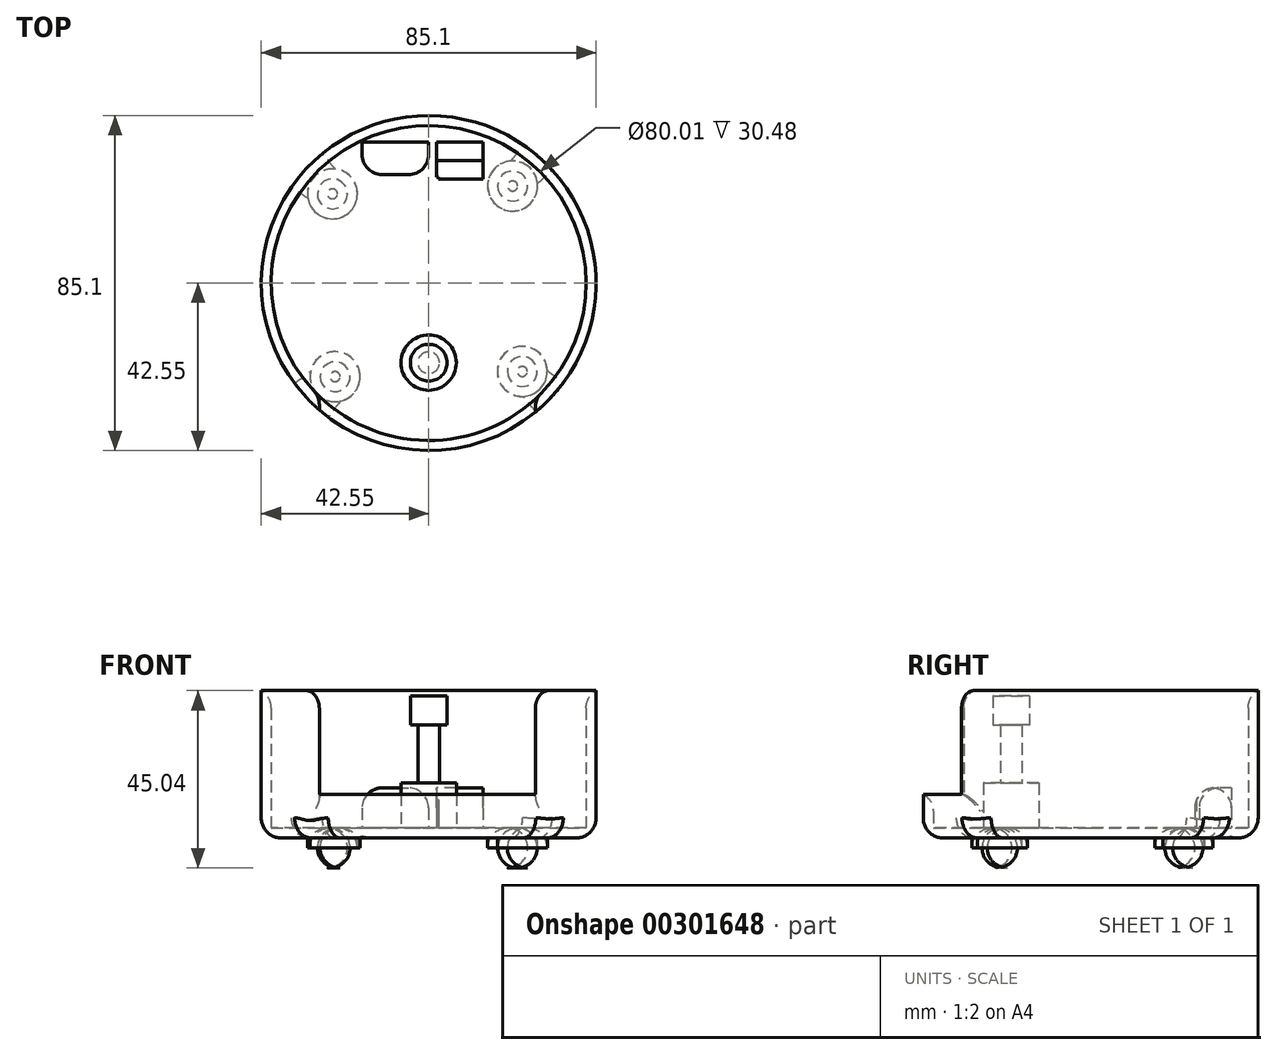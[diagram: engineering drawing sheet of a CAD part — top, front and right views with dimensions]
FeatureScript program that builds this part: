
annotation { "Feature Type Name" : "Feature", "Feature Type Description" : "" }
export const myFeature = defineFeature(function(context is Context, id is Id, definition is map)
    precondition{}
    {
        {
            var Q0;
            Q0=qCreatedBy(makeId("Top.planeOp"),FACE);
            var sketch = newSketch(context, id + "F0", { "sketchPlane" : qUnion([Q0])});
            skCircle(sketch, "E0", {"center": v(0, 0) * mm, "radius": 42.55 * mm});
            skSolve(sketch);
        }
        {
            var Q0;
            Q0 = qSketchRegion(id + "F0", true);
            extrude(context, id + "F1", {"entities" : qUnion([Q0]), "depth" : 38.1 * mm});
        }
        {
            var Q0;
            Q0=makeQuery(id+"F1.opExtrude","CAP_FACE",FACE,{"disambiguationData":[OSD([sQuery(id+"F0.wireOp",EDGE,"E0")])],"isStart":false});
            shell(context, id + "F2", {"entities" : qUnion([Q0]), "thickness" : 2.54 * mm});
        }
        {
            var Q0;
            Q0=qCreatedBy(makeId("Top.planeOp"),FACE);
            var sketch = newSketch(context, id + "F3", { "sketchPlane" : qUnion([Q0])});
            skCircle(sketch, "E1", {"center": v(-23.78, -23.78) * mm, "radius": 6.35 * mm});
            skCircle(sketch, "E2", {"center": v(23.78, -22.45) * mm, "radius": 6.35 * mm});
            skCircle(sketch, "E3", {"center": v(21.34, 24.67) * mm, "radius": 6.35 * mm});
            skCircle(sketch, "E4", {"center": v(-24.45, 22.67) * mm, "radius": 6.35 * mm});
            skSolve(sketch);
        }
        {
            var Q0;
            Q0 = qSketchRegion(id + "F3", true);
            extrude(context, id + "F4", {"entities" : qUnion([Q0]), "operationType" : NewBodyOperationType.ADD, "oppositeDirection" : true, "depth" : 7.62 * mm});
        }
        {
            var Q0;
            Q0=makeQuery(id+"F4.opExtrude","CAP_EDGE",EDGE,{"disambiguationData":[OSD([sQuery(id+"F3.wireOp",EDGE,"E1")])],"isStart":false});
            var Q1;
            Q1=makeQuery(id+"F4.opExtrude","CAP_EDGE",EDGE,{"disambiguationData":[OSD([sQuery(id+"F3.wireOp",EDGE,"E2")])],"isStart":false});
            var Q2;
            Q2=makeQuery(id+"F4.opExtrude","CAP_EDGE",EDGE,{"disambiguationData":[OSD([sQuery(id+"F3.wireOp",EDGE,"E3")])],"isStart":false});
            var Q3;
            Q3=makeQuery(id+"F4.opExtrude","CAP_EDGE",EDGE,{"disambiguationData":[OSD([sQuery(id+"F3.wireOp",EDGE,"E4")])],"isStart":false});
            fillet(context, id + "F5", {"entities" : qUnion([Q0, Q1, Q2, Q3]), "radius" : 5.08 * mm, "tangentPropagation" : true, "allowEdgeOverflow" : false});
        }
        {
            var Q0;
            Q0=qCreatedBy(makeId("Front.planeOp"),FACE);
            cPlane(context, id + "F6", {"entities" : qUnion([Q0]), "cplaneType" : CPlaneType.OFFSET, "offset" : 69.34 * mm, "width" : 152.4 * mm, "height" : 152.4 * mm});
        }
        {
            var Q0;
            Q0=qCreatedBy(id+"F6.planeOp",FACE);
            var sketch = newSketch(context, id + "F7", { "sketchPlane" : qUnion([Q0])});
            skLineSegment(sketch, "E5.bottom", {"start": v(-27.78, 42.9) * mm, "end": v(27.11, 42.9) * mm});
            skLineSegment(sketch, "E5.top", {"start": v(-27.78, 11.11) * mm, "end": v(27.11, 11.11) * mm});
            skLineSegment(sketch, "E5.left", {"start": v(-27.78, 42.9) * mm, "end": v(-27.78, 11.11) * mm});
            skLineSegment(sketch, "E5.right", {"start": v(27.11, 42.9) * mm, "end": v(27.11, 11.11) * mm});
            skSolve(sketch);
        }
        {
            var Q0;
            Q0 = qSketchRegion(id + "F7", true);
            extrude(context, id + "F8", {"entities" : qUnion([Q0]), "operationType" : NewBodyOperationType.REMOVE, "oppositeDirection" : true, "depth" : 55.12 * mm});
        }
        {
            var Q0;
            {var subQ0=sQuery(id+"F0.wireOp",EDGE,"E0");Q0=makeQuery(id+"F8.boolean.opBoolean","INTERSECT",EDGE,{"derivedFrom":[makeQuery(id+"F2.opShell","OFFSET_FACE",FACE,{"disambiguationData":[OSD([subQ0]),TDD([makeQuery(id+"F1.opExtrude","SWEPT_FACE",FACE,{"disambiguationData":[OSD([subQ0])]})])]}),makeQuery(id+"F8.opExtrude","SWEPT_FACE",FACE,{"disambiguationData":[OSD([sQuery(id+"F7.wireOp",EDGE,"E5.top")])]})]});}
            var Q1;
            {var subQ0=sQuery(id+"F0.wireOp",EDGE,"E0");Q1=makeQuery(id+"F8.boolean.opBoolean","INTERSECT",EDGE,{"derivedFrom":[makeQuery(id+"F2.opShell","OFFSET_FACE",FACE,{"disambiguationData":[OSD([subQ0]),TDD([makeQuery(id+"F1.opExtrude","SWEPT_FACE",FACE,{"disambiguationData":[OSD([subQ0])]})])]}),makeQuery(id+"F8.opExtrude","SWEPT_FACE",FACE,{"disambiguationData":[OSD([sQuery(id+"F7.wireOp",EDGE,"E5.left")])]})]});}
            var Q2;
            {var subQ0=sQuery(id+"F0.wireOp",EDGE,"E0");Q2=makeQuery(id+"F8.boolean.opBoolean","INTERSECT",EDGE,{"derivedFrom":[makeQuery(id+"F2.opShell","OFFSET_FACE",FACE,{"disambiguationData":[OSD([subQ0]),TDD([makeQuery(id+"F1.opExtrude","SWEPT_FACE",FACE,{"disambiguationData":[OSD([subQ0])]})])]}),makeQuery(id+"F8.opExtrude","SWEPT_FACE",FACE,{"disambiguationData":[OSD([sQuery(id+"F7.wireOp",EDGE,"E5.right")])]})]});}
            fillet(context, id + "F9", {"entities" : qUnion([Q0, Q1, Q2]), "radius" : 5.08 * mm, "tangentPropagation" : true, "allowEdgeOverflow" : false});
        }
        {
            var Q0;
            {var subQ0=sQuery(id+"F0.wireOp",EDGE,"E0");Q0=makeQuery(id+"F2.opShell","OFFSET_EDGE",EDGE,{"disambiguationData":[OSD([subQ0]),TDD([makeQuery(id+"F1.opExtrude","CAP_EDGE",EDGE,{"disambiguationData":[OSD([subQ0])],"isStart":false})])]});}
            fillet(context, id + "F10", {"entities" : qUnion([Q0]), "radius" : 5.08 * mm, "tangentPropagation" : true, "allowEdgeOverflow" : false});
        }
        {
            var Q0;
            Q0=makeQuery(id+"F1.opExtrude","CAP_EDGE",EDGE,{"disambiguationData":[OSD([sQuery(id+"F0.wireOp",EDGE,"E0")])],"isStart":true});
            fillet(context, id + "F11", {"entities" : qUnion([Q0]), "radius" : 5.08 * mm, "tangentPropagation" : true, "allowEdgeOverflow" : false});
        }
        {
            var Q0;
            Q0=qCreatedBy(makeId("Top.planeOp"),FACE);
            var sketch = newSketch(context, id + "F12", { "sketchPlane" : qUnion([Q0])});
            skLineSegment(sketch, "E6.bottom", {"start": v(-16.9, 35.78) * mm, "end": v(0, 35.78) * mm});
            skLineSegment(sketch, "E6.top", {"start": v(-16.9, 27.56) * mm, "end": v(0, 27.56) * mm});
            skLineSegment(sketch, "E6.left", {"start": v(-16.9, 35.78) * mm, "end": v(-16.9, 27.56) * mm});
            skLineSegment(sketch, "E6.right", {"start": v(0, 35.78) * mm, "end": v(0, 27.56) * mm});
            skLineSegment(sketch, "E7.bottom", {"start": v(2, 35.78) * mm, "end": v(13.78, 35.78) * mm});
            skLineSegment(sketch, "E7.top", {"start": v(2, 35.34) * mm, "end": v(13.78, 35.34) * mm});
            skLineSegment(sketch, "E7.left", {"start": v(2, 35.78) * mm, "end": v(2, 35.34) * mm});
            skLineSegment(sketch, "E7.right", {"start": v(13.78, 35.78) * mm, "end": v(13.78, 35.34) * mm});
            skLineSegment(sketch, "E8.bottom", {"start": v(13.78, 26.45) * mm, "end": v(2.44, 26.45) * mm});
            skLineSegment(sketch, "E8.top", {"start": v(13.78, 26.9) * mm, "end": v(2.44, 26.9) * mm});
            skLineSegment(sketch, "E8.left", {"start": v(13.78, 26.45) * mm, "end": v(13.78, 26.9) * mm});
            skLineSegment(sketch, "E8.right", {"start": v(2.44, 26.45) * mm, "end": v(2.44, 26.9) * mm});
            skLineSegment(sketch, "E9.top", {"start": v(2, 26.9) * mm, "end": v(13.78, 26.9) * mm});
            skLineSegment(sketch, "E9.left", {"start": v(2, 35.34) * mm, "end": v(2, 26.9) * mm});
            skLineSegment(sketch, "E9.right", {"start": v(13.78, 35.34) * mm, "end": v(13.78, 26.9) * mm});
            skSolve(sketch);
        }
        {
            var Q0;
            Q0 = qSketchRegion(id + "F12", true);
            extrude(context, id + "F13", {"entities" : qUnion([Q0]), "operationType" : NewBodyOperationType.ADD, "depth" : 12.7 * mm});
        }
        {
            var Q0;
            Q0=makeQuery(id+"F13.opExtrude","CAP_EDGE",EDGE,{"disambiguationData":[OSD([sQuery(id+"F12.wireOp",EDGE,"E6.top")])],"isStart":false});
            var Q1;
            Q1=makeQuery(id+"F13.opExtrude","SWEPT_EDGE",EDGE,{"disambiguationData":[OSD([sQuery(id+"F12.wireOp",EDGE,"E6.top"),sQuery(id+"F12.wireOp",EDGE,"E6.right")])]});
            var Q2;
            Q2=makeQuery(id+"F13.opExtrude","SWEPT_EDGE",EDGE,{"disambiguationData":[OSD([sQuery(id+"F12.wireOp",EDGE,"E6.top"),sQuery(id+"F12.wireOp",EDGE,"E6.left")])]});
            var Q3;
            Q3=makeQuery(id+"F13.opExtrude","CAP_EDGE",EDGE,{"disambiguationData":[OSD([sQuery(id+"F12.wireOp",EDGE,"E6.left")])],"isStart":false});
            var Q4;
            Q4=makeQuery(id+"F13.opExtrude","CAP_EDGE",EDGE,{"disambiguationData":[OSD([sQuery(id+"F12.wireOp",EDGE,"E6.right")])],"isStart":false});
            fillet(context, id + "F14", {"entities" : qUnion([Q0, Q1, Q2, Q3, Q4]), "radius" : 5.08 * mm, "tangentPropagation" : true, "allowEdgeOverflow" : false});
        }
        {
            var Q0;
            Q0=makeQuery(id+"F13.opExtrude","CAP_EDGE",EDGE,{"disambiguationData":[OSD([sQuery(id+"F12.wireOp",EDGE,"E8.bottom")])],"isStart":false});
            var Q1;
            Q1=makeQuery(id+"F13.opExtrude","CAP_EDGE",EDGE,{"disambiguationData":[OSD([sQuery(id+"F12.wireOp",EDGE,"E7.bottom")])],"isStart":false});
            fillet(context, id + "F15", {"entities" : qUnion([Q0, Q1]), "radius" : 5.08 * mm, "tangentPropagation" : true, "allowEdgeOverflow" : false});
        }
        {
            var Q0;
            {var subQ0=sQuery(id+"F0.wireOp",EDGE,"E0");Q0=makeQuery(id+"F2.opShell","OFFSET_FACE",FACE,{"disambiguationData":[OSD([subQ0]),TDD([makeQuery(id+"F1.opExtrude","CAP_FACE",FACE,{"disambiguationData":[OSD([subQ0])],"isStart":true})])]});}
            var sketch = newSketch(context, id + "F16", { "sketchPlane" : qUnion([Q0])});
            skCircle(sketch, "E10", {"center": v(0, -20.22) * mm, "radius": 7.03 * mm});
            skSolve(sketch);
        }
        {
            var Q0;
            Q0 = qSketchRegion(id + "F16", true);
            extrude(context, id + "F17", {"entities" : qUnion([Q0]), "operationType" : NewBodyOperationType.ADD, "depth" : 11.43 * mm});
        }
        {
            var Q0;
            Q0=makeQuery(id+"F17.opExtrude","CAP_FACE",FACE,{"disambiguationData":[OSD([sQuery(id+"F16.wireOp",EDGE,"E10")])],"isStart":false});
            var sketch = newSketch(context, id + "F18", { "sketchPlane" : qUnion([Q0])});
            skCircle(sketch, "E11", {"center": v(0, -20.22) * mm, "radius": 2.75 * mm});
            skSolve(sketch);
        }
        {
            var Q0;
            Q0 = qSketchRegion(id + "F18", true);
            extrude(context, id + "F19", {"entities" : qUnion([Q0]), "operationType" : NewBodyOperationType.ADD, "depth" : 14.73 * mm});
        }
        {
            var Q0;
            Q0=makeQuery(id+"F19.opExtrude","CAP_FACE",FACE,{"disambiguationData":[OSD([sQuery(id+"F18.wireOp",EDGE,"E11")])],"isStart":false});
            var sketch = newSketch(context, id + "F20", { "sketchPlane" : qUnion([Q0])});
            skCircle(sketch, "E12", {"center": v(0, -20.22) * mm, "radius": 4.67 * mm});
            skSolve(sketch);
        }
        {
            var Q0;
            Q0 = qSketchRegion(id + "F20", true);
            extrude(context, id + "F21", {"entities" : qUnion([Q0]), "operationType" : NewBodyOperationType.ADD, "depth" : 7.37 * mm});
        }
    });
